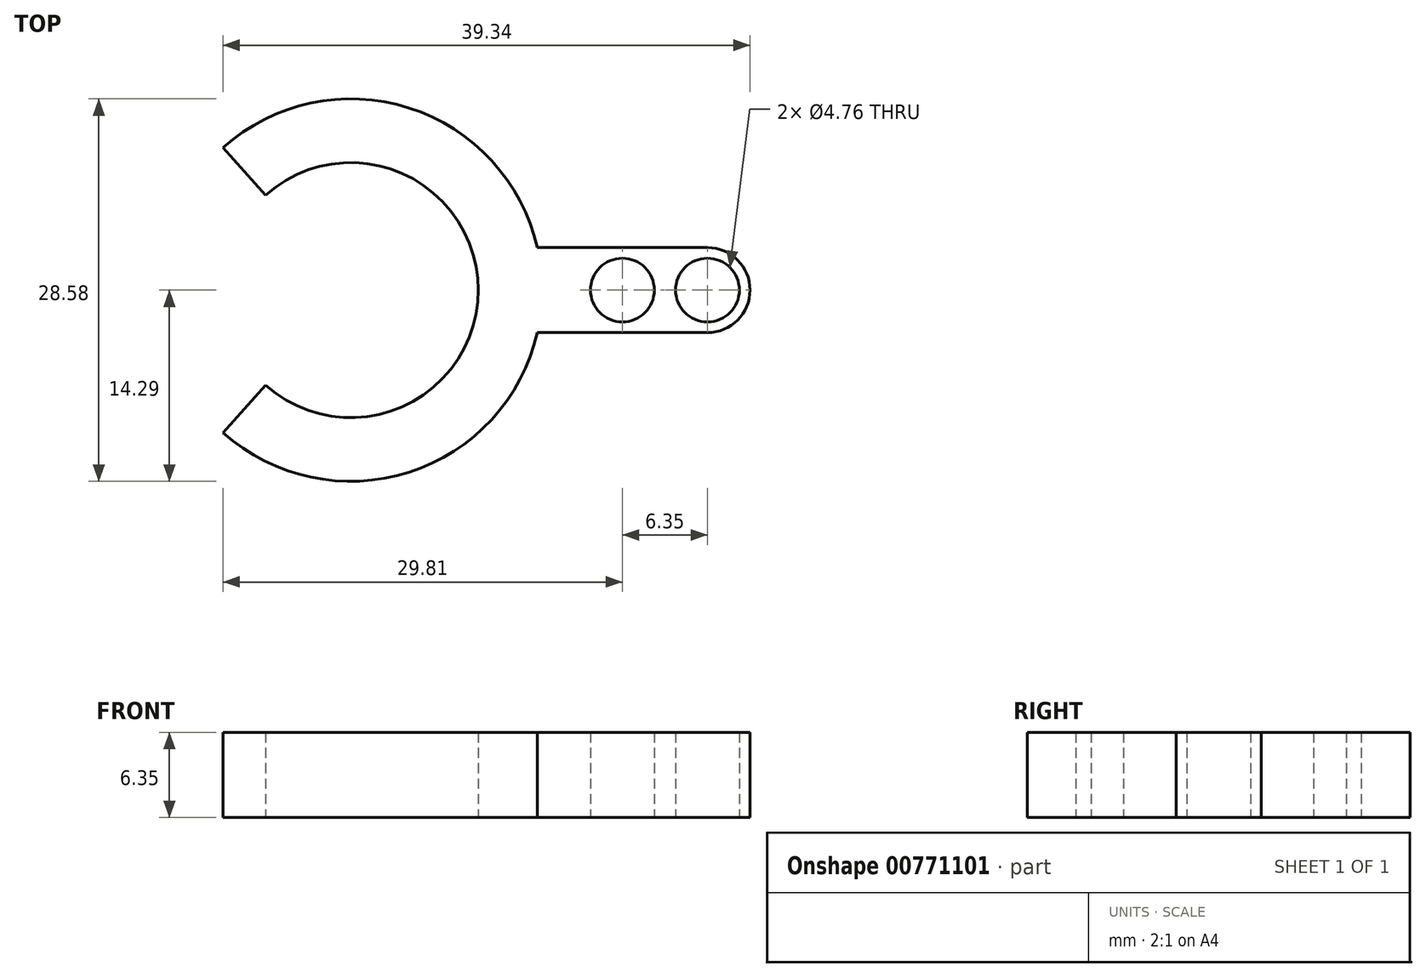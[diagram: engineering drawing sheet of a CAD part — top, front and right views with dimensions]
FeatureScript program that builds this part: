
annotation { "Feature Type Name" : "Feature", "Feature Type Description" : "" }
export const myFeature = defineFeature(function(context is Context, id is Id, definition is map)
    precondition{}
    {
        {
            var Q0;
            Q0=qCreatedBy(makeId("Top.planeOp"),FACE);
            var sketch = newSketch(context, id + "F0", { "sketchPlane" : qUnion([Q0])});
            skArc(sketch, "E0", {"start": v(-6.35, 7.1) * mm, "mid": v(9.53, 0) * mm, "end": v(-6.35, -7.1) * mm});
            skArc(sketch, "E1", {"start": v(-9.53, 10.65) * mm, "mid": v(14.29, 0) * mm, "end": v(-9.53, -10.65) * mm});
            skLineSegment(sketch, "E2", {"start": v(-9.53, -10.65) * mm, "end": v(-6.35, -7.1) * mm});
            skLineSegment(sketch, "E3", {"start": v(-9.52, 10.65) * mm, "end": v(-6.35, 7.1) * mm});
            skSolve(sketch);
        }
        {
            var Q0;
            Q0 = qSketchRegion(id + "F0", true);
            extrude(context, id + "F1", {"entities" : qUnion([Q0]), "depth" : 6.35 * mm, "offsetDistance" : 25.4 * mm});
        }
        {
            var Q0;
            Q0=qCreatedBy(makeId("Top.planeOp"),FACE);
            var sketch = newSketch(context, id + "F2", { "sketchPlane" : qUnion([Q0])});
            skLineSegment(sketch, "E4", {"start": v(13.93, 3.18) * mm, "end": v(26.63, 3.18) * mm});
            skLineSegment(sketch, "E5", {"start": v(13.93, -3.17) * mm, "end": v(26.63, -3.17) * mm});
            skArc(sketch, "E6", {"start": v(26.63, 3.18) * mm, "mid": v(29.8, 0) * mm, "end": v(26.63, -3.18) * mm});
            skCircle(sketch, "E7", {"center": v(26.63, 0) * mm, "radius": 2.38 * mm});
            skCircle(sketch, "E8", {"center": v(20.28, 0) * mm, "radius": 2.38 * mm});
            skArc(sketch, "E9", {"start": v(13.93, -3.17) * mm, "mid": v(14.29, 0) * mm, "end": v(13.93, 3.17) * mm});
            skSolve(sketch);
        }
        {
            var Q0;
            Q0 = qSketchRegion(id + "F2", true);
            var Q1;
            Q1=makeQuery(id+"F1.opExtrude","CAP_FACE",FACE,{"disambiguationData":[OSD([sQuery(id+"F0.wireOp",EDGE,"E0"),sQuery(id+"F0.wireOp",EDGE,"E1"),sQuery(id+"F0.wireOp",EDGE,"E2"),sQuery(id+"F0.wireOp",EDGE,"E3")])],"isStart":false});
            extrude(context, id + "F3", {"entities" : qUnion([Q0]), "operationType" : NewBodyOperationType.ADD, "endBound" : BoundingType.UP_TO_SURFACE, "depth" : 25.4 * mm, "endBoundEntityFace" : qUnion([Q1]), "offsetDistance" : 25.4 * mm});
        }
    });
